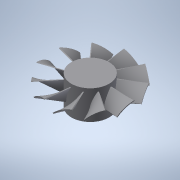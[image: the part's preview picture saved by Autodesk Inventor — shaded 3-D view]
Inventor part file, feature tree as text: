
AUTODESK INVENTOR PART (.ipt)
format: ipt  version: 2020 (Build 240168000, 168)  size: 458,752 bytes
history: native  units: mm
features: sketch x6, plane x4, extrude x2, other x1, loft x1, pattern_circular x1
ambient origin geometry x8: Origin, YZ Plane, XZ Plane, XY Plane, X Axis, Y Axis, Z Axis, Center Point
bodies: Body1 (feature_tree)
feature tree (15):
  other  "實體1"
  extrude  "擠出1"  Depth=21.7mm
  sketch  "草圖3"
  plane  "工作平面1"
  plane  "工作平面2"
  sketch  "草圖2"
  sketch  "草圖4"
  plane  "工作平面3"
  sketch  "草圖5"
  plane  "工作平面4"
  sketch  "草圖6"
  loft  "斷面混成1"
  extrude  "擠出2"  Depth=2.0mm
  pattern_circular  "環形陣列1"  [2 undecoded]
  sketch  "草圖1"
note: 2 required parameter values undecoded (feature->parameter linkage not recoverable at this tier; creation-order binding heuristic only, values carry confidence <= 0.55)
